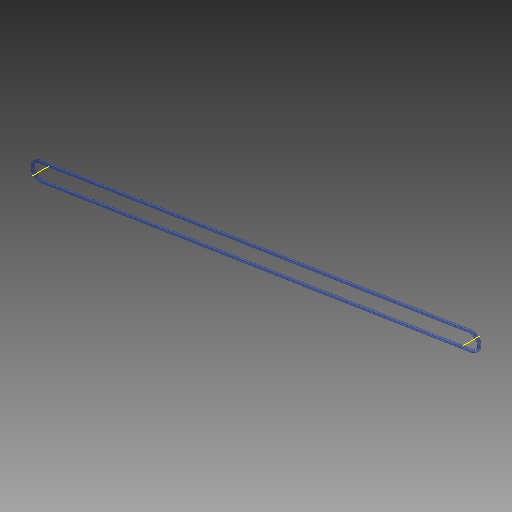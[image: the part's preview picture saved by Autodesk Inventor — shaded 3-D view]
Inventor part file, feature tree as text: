
AUTODESK INVENTOR PART (.ipt)
format: ipt  version: 2017 (Build 210142000, 142)  size: 135,680 bytes
history: native  units: mm
features: other x5, plane x2, pattern_linear x1
ambient origin geometry x8: Origin, YZ Plane, XZ Plane, XY Plane, X Axis, Y Axis, Z Axis, Center Point
bodies: Solid1 (feature_tree), Solid (feature_tree)
feature tree (8):
  other  "Work Axis1"
  other  "Work Axis2"
  plane  "Work Plane2"
  plane  "Work Plane3"
  other  "Path"
  other  "Section Plane"
  pattern_linear  "Strand Pattern"  Spacing1=0.0mm  [1 undecoded]
  other  "Section Sketch"
note: 1 required parameter value undecoded (feature->parameter linkage not recoverable at this tier; creation-order binding heuristic only, values carry confidence <= 0.55)
